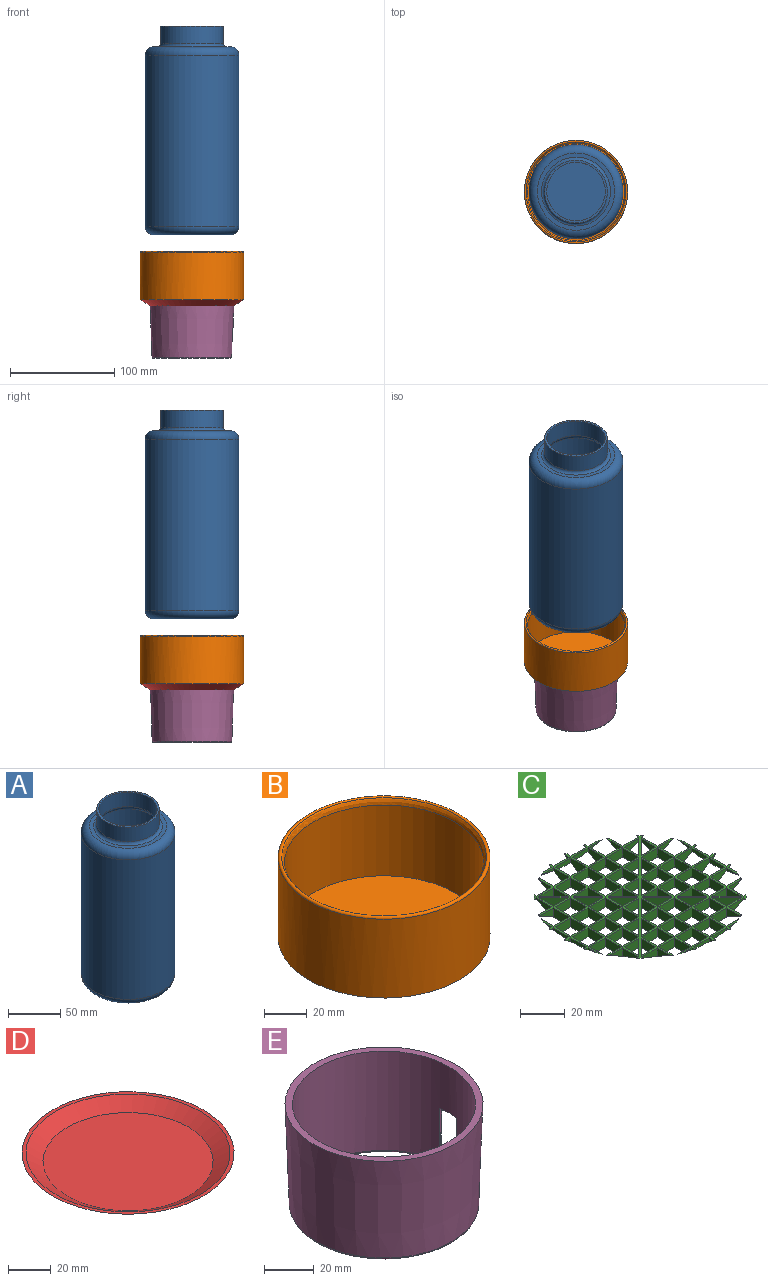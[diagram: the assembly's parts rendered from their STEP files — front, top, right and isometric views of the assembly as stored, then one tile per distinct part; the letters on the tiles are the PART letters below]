
ASSEMBLY  parts=5 mates=4
PART A: 15 faces, bbox 97.4x97.4x200 mm
  f0: plane 74x74mm, normal (0,0,-1), area 879.6mm2, adj f1,f14
  f1: revolved ~86x86mm, area 2359mm2, adj f0,f2
  f2: cylinder r=43mm len=164mm, axis (0,0,1), area 44309mm2, adj f1,f3
  f3: torus R=37mm, axis (0,0,1), area 2417.2mm2, adj f2,f4
  f4: plane 74x74mm, normal (0,0,1), area 4300.8mm2, adj f3
  f5: plane 74x74mm, normal (0,0,-1), area 4300.8mm2, adj f6
  f6: torus R=37mm, axis (0,0,1), area 3323.5mm2, adj f5,f7
  f7: cylinder r=45mm len=164mm, axis (0,0,1), area 46369.9mm2, adj f6,f8
  f8: torus R=37mm, axis (0,0,1), area 3323.5mm2, adj f7,f9
  f9: plane 74x74mm, normal (0,0,1), area 879.6mm2, adj f8,f10
  f10: torus R=33mm, axis (0,0,1), area 920.5mm2, adj f9,f11
  f11: cylinder r=30mm len=60mm, axis (0,0,1), area 3204.4mm2, adj f10,f12
  f12: plane 60x60mm, normal (0,0,1), area 364.4mm2, adj f11,f13
  f13: cylinder r=28mm len=56mm, axis (0,0,1), area 2990.8mm2, adj f12,f14
  f14: torus R=33mm, axis (0,0,1), area 1471.4mm2, adj f0,f13
PART B: 6 faces, bbox 107.2x107.2x46.1 mm
  f0: plane 99x99mm, normal (0,0,-1), area 7697.7mm2, adj f1
  f1: cylinder r=49.5mm len=99mm, axis (0,0,1), area 14015.4mm2, adj f0,f5
  f2: cylinder r=46.5mm len=93mm, axis (0,0,1), area 11808.7mm2, adj f3,f4
  f3: plane 93x93mm, normal (0,0,1), area 6792.9mm2, adj f2
  f4: torus R=51.5mm, axis (0,0,1), area 1065.4mm2, adj f2,f5
  f5: torus R=48.5mm, axis (0,0,-1), area 741.3mm2, adj f1,f4
PART C: 306 faces, bbox 95.5x95.5x5.2 mm
  f0: plane 95.25x95.25mm, normal (0,0,1), area 1422.5mm2, adj f2,f3,f4,f5,f6,f7,f8,f9
  f1: plane 79.42x79.42mm, normal (0,0,-1), area 1003.4mm2, adj f66,f67,f69,f70,f71,f72,f73,f74
  f2: plane 1.96x1.21mm, normal (0,-1,0), area 1.2mm2, adj f0,f297,f298
  f3: plane 1.73x1.06mm, normal (0,1,0), area 0.9mm2, adj f0,f4,f298
  f4: plane 5.68x1.26mm, normal (1,0,0), area 3mm2, adj f0,f3,f298
  f5: plane 8.48x4.6mm, normal (0,1,0), area 19.7mm2, adj f0,f6,f299
  f6: plane 10.01x4.6mm, normal (1,0,0), area 26.7mm2, adj f0,f5,f7,f299
  f7: plane 1.33x0.61mm, normal (0,-1,0), area 0.4mm2, adj f0,f6,f299
  f8: plane 1.33x0.61mm, normal (-1,0,0), area 0.4mm2, adj f0,f9,f299
  f9: plane 10.01x4.6mm, normal (0,1,0), area 26.7mm2, adj f0,f8,f10,f299
  f10: plane 8.48x4.6mm, normal (1,0,0), area 19.7mm2, adj f0,f9,f299
  f11: plane 5.68x1.26mm, normal (0,1,0), area 3mm2, adj f0,f12,f300
  f12: plane 1.73x1.06mm, normal (1,0,0), area 0.9mm2, adj f0,f11,f300
  f13: plane 1.96x1.21mm, normal (-1,0,0), area 1.2mm2, adj f0,f14,f300
  f14: plane 10.01x1.98mm, normal (0,1,0), area 17mm2, adj f0,f13,f15,f300
  f15: plane 3.13x1.97mm, normal (1,0,0), area 3.1mm2, adj f0,f14,f300
  f16: plane 3.13x1.97mm, normal (-1,0,0), area 3.1mm2, adj f0,f17,f300
  f17: plane 10.01x1.98mm, normal (0,1,0), area 17mm2, adj f0,f16,f18,f300
  f18: plane 1.96x1.21mm, normal (1,0,0), area 1.2mm2, adj f0,f17,f300
  f19: plane 1.73x1.06mm, normal (-1,0,0), area 0.9mm2, adj f0,f20,f300
  f20: plane 5.68x1.26mm, normal (0,1,0), area 3mm2, adj f0,f19,f300
  f21: plane 8.48x4.6mm, normal (-1,0,0), area 19.7mm2, adj f0,f22,f301
  f22: plane 10.01x4.6mm, normal (0,1,0), area 26.7mm2, adj f0,f21,f23,f301
  f23: plane 1.33x0.61mm, normal (1,0,0), area 0.4mm2, adj f0,f22,f301
  f24: plane 1.33x0.61mm, normal (0,-1,0), area 0.4mm2, adj f0,f25,f301
  f25: plane 10.01x4.6mm, normal (-1,0,0), area 26.7mm2, adj f0,f24,f26,f301
  f26: plane 8.48x4.6mm, normal (0,1,0), area 19.7mm2, adj f0,f25,f301
  f27: plane 5.68x1.26mm, normal (-1,0,0), area 3mm2, adj f0,f28,f302
  f28: plane 1.73x1.06mm, normal (0,1,0), area 0.9mm2, adj f0,f27,f302
  f29: plane 1.96x1.21mm, normal (0,-1,0), area 1.2mm2, adj f0,f30,f302
  f30: plane 10.01x1.98mm, normal (-1,0,0), area 17mm2, adj f0,f29,f31,f302
  f31: plane 3.13x1.97mm, normal (0,1,0), area 3.1mm2, adj f0,f30,f302
  f32: plane 3.13x1.97mm, normal (0,-1,0), area 3.1mm2, adj f0,f33,f302
  f33: plane 10.01x1.98mm, normal (-1,0,0), area 17mm2, adj f0,f32,f34,f302
  f34: plane 1.96x1.21mm, normal (0,1,0), area 1.2mm2, adj f0,f33,f302
  f35: plane 1.73x1.06mm, normal (0,-1,0), area 0.9mm2, adj f0,f36,f302
  f36: plane 5.68x1.26mm, normal (-1,0,0), area 3mm2, adj f0,f35,f302
  f37: plane 8.48x4.6mm, normal (0,-1,0), area 19.7mm2, adj f0,f38,f303
  f38: plane 10.01x4.6mm, normal (-1,0,0), area 26.7mm2, adj f0,f37,f39,f303
  f39: plane 1.33x0.61mm, normal (0,1,0), area 0.4mm2, adj f0,f38,f303
  f40: plane 1.33x0.61mm, normal (1,0,0), area 0.4mm2, adj f0,f41,f303
  f41: plane 10.01x4.6mm, normal (0,-1,0), area 26.7mm2, adj f0,f40,f42,f303
  f42: plane 8.48x4.6mm, normal (-1,0,0), area 19.7mm2, adj f0,f41,f303
  f43: plane 5.68x1.26mm, normal (0,-1,0), area 3mm2, adj f0,f44,f304
  f44: plane 1.73x1.06mm, normal (-1,0,0), area 0.9mm2, adj f0,f43,f304
  f45: plane 1.96x1.21mm, normal (1,0,0), area 1.2mm2, adj f0,f46,f304
  f46: plane 10.01x1.98mm, normal (0,-1,0), area 17mm2, adj f0,f45,f47,f304
  f47: plane 3.13x1.97mm, normal (-1,0,0), area 3.1mm2, adj f0,f46,f304
  f48: plane 3.13x1.97mm, normal (1,0,0), area 3.1mm2, adj f0,f49,f304
  f49: plane 10.01x1.98mm, normal (0,-1,0), area 17mm2, adj f0,f48,f50,f304
  f50: plane 1.96x1.21mm, normal (-1,0,0), area 1.2mm2, adj f0,f49,f304
  f51: plane 1.73x1.06mm, normal (1,0,0), area 0.9mm2, adj f0,f52,f304
  f52: plane 5.68x1.26mm, normal (0,-1,0), area 3mm2, adj f0,f51,f304
  f53: plane 8.48x4.6mm, normal (1,0,0), area 19.7mm2, adj f0,f54,f305
  f54: plane 10.01x4.6mm, normal (0,-1,0), area 26.7mm2, adj f0,f53,f55,f305
  f55: plane 1.33x0.61mm, normal (-1,0,0), area 0.4mm2, adj f0,f54,f305
  f56: plane 1.33x0.61mm, normal (0,1,0), area 0.4mm2, adj f0,f57,f305
  f57: plane 10.01x4.6mm, normal (1,0,0), area 26.7mm2, adj f0,f56,f58,f305
  f58: plane 8.48x4.6mm, normal (0,-1,0), area 19.7mm2, adj f0,f57,f305
  f59: plane 5.68x1.26mm, normal (1,0,0), area 3mm2, adj f0,f60,f298
  f60: plane 1.73x1.06mm, normal (0,-1,0), area 0.9mm2, adj f0,f59,f298
  f61: plane 1.96x1.21mm, normal (0,1,0), area 1.2mm2, adj f0,f62,f298
  f62: plane 10.01x1.98mm, normal (1,0,0), area 17mm2, adj f0,f61,f63,f298
  f63: plane 3.13x1.97mm, normal (0,-1,0), area 3.1mm2, adj f0,f62,f298
  f64: plane 3.13x1.97mm, normal (0,1,0), area 3.1mm2, adj f0,f297,f298
  f65: plane 7.91x1.68mm, normal (0,1,0), area 7.1mm2, adj f0,f66,f304
  f66: plane 10.1x5.1mm, normal (1,0,0), area 40.9mm2, adj f0,f1,f65,f67,f304
  f67: plane 10x5mm, normal (0,-1,0), area 50mm2, adj f0,f1,f66,f233,f305
  f68: plane 10.01x2.61mm, normal (0,1,0), area 23.3mm2, adj f0,f69,f234,f304
  f69: plane 10.08x5.08mm, normal (1,0,0), area 41.7mm2, adj f0,f1,f68,f70,f304
  f70: plane 10x5mm, normal (0,-1,0), area 50mm2, adj f0,f1,f69,f234
  f71: plane 9.3x9.3mm, normal (-0.71,0.71,0), area 55.3mm2, adj f0,f1,f72,f235,f303
  f72: plane 9.3x5.01mm, normal (1,0,0), area 30.7mm2, adj f0,f1,f71,f235,f303
  f73: plane 9.3x5.01mm, normal (0,1,0), area 30.7mm2, adj f0,f1,f74,f236,f303
  f74: plane 9.3x9.3mm, normal (0.71,-0.71,0), area 55.3mm2, adj f0,f1,f73,f236,f303
  f75: plane 10x5mm, normal (1,0,0), area 50mm2, adj f0,f1,f76,f237
  f76: plane 10x5mm, normal (0,-1,0), area 50mm2, adj f0,f1,f75,f77
  f77: plane 10x5mm, normal (-1,0,0), area 50mm2, adj f0,f1,f76,f237
  f78: plane 10x5mm, normal (-1,0,0), area 50mm2, adj f0,f1,f79,f238
  f79: plane 10x5mm, normal (0,1,0), area 50mm2, adj f0,f1,f78,f80
  f80: plane 10x5mm, normal (1,0,0), area 50mm2, adj f0,f1,f79,f238
  f81: plane 10x5mm, normal (1,0,0), area 50mm2, adj f0,f1,f82,f239
  f82: plane 10x5mm, normal (0,-1,0), area 50mm2, adj f0,f1,f81,f83
  f83: plane 10x5mm, normal (-1,0,0), area 50mm2, adj f0,f1,f82,f239
  f84: plane 9.3x5mm, normal (0,1,0), area 30.7mm2, adj f0,f1,f85,f240,f305
  f85: plane 9.29x5mm, normal (1,0,0), area 46.5mm2, adj f0,f1,f84,f240
  f86: plane 9x4.94mm, normal (0,1,0), area 22.4mm2, adj f0,f87,f305
  f87: plane 10x5mm, normal (1,0,0), area 50mm2, adj f0,f1,f86,f88,f305
  f88: plane 10.1x5.1mm, normal (0,-1,0), area 40.9mm2, adj f0,f1,f87,f241,f298
  f89: plane 10x5mm, normal (0,1,0), area 50mm2, adj f0,f1,f90,f242
  f90: plane 10x5mm, normal (1,0,0), area 50mm2, adj f0,f1,f89,f91
  f91: plane 10x5mm, normal (0,-1,0), area 50mm2, adj f0,f1,f90,f242
  f92: plane 9.29x5mm, normal (0,1,0), area 46.5mm2, adj f0,f1,f93,f243
  f93: plane 9.29x5mm, normal (1,0,0), area 46.5mm2, adj f0,f1,f92,f243
  f94: plane 9.29x5mm, normal (0,1,0), area 46.5mm2, adj f0,f1,f95,f244
  f95: plane 9.29x9.29mm, normal (0.71,-0.71,0), area 65.7mm2, adj f0,f1,f94,f244
  f96: plane 9.29x5mm, normal (-1,0,0), area 46.5mm2, adj f0,f1,f97,f245
  f97: plane 9.29x5mm, normal (0,1,0), area 46.5mm2, adj f0,f1,f96,f245
  f98: plane 10x5mm, normal (0,1,0), area 50mm2, adj f0,f1,f99,f246
  f99: plane 10x5mm, normal (1,0,0), area 50mm2, adj f0,f1,f98,f100
  f100: plane 10x5mm, normal (0,-1,0), area 50mm2, adj f0,f1,f99,f246
  f101: plane 9.29x9.29mm, normal (-0.71,0.71,0), area 65.7mm2, adj f0,f1,f102,f247
  f102: plane 9.29x5mm, normal (1,0,0), area 46.5mm2, adj f0,f1,f101,f247
  f103: plane 10x5mm, normal (0,1,0), area 50mm2, adj f0,f1,f104,f248
  f104: plane 10x5mm, normal (1,0,0), area 50mm2, adj f0,f1,f103,f105
  f105: plane 10x5mm, normal (0,-1,0), area 50mm2, adj f0,f1,f104,f248
  f106: plane 9x4.94mm, normal (0,1,0), area 22.4mm2, adj f0,f249,f303
  f107: plane 7.91x1.68mm, normal (1,0,0), area 7.1mm2, adj f0,f108,f302
  f108: plane 10.1x5.1mm, normal (0,-1,0), area 40.9mm2, adj f0,f1,f107,f249,f302
  f109: plane 10.08x5.08mm, normal (0,1,0), area 41.7mm2, adj f0,f1,f110,f250,f302
  f110: plane 10.01x2.61mm, normal (1,0,0), area 23.3mm2, adj f0,f109,f111,f302
  f111: plane 10x5mm, normal (0,-1,0), area 45.5mm2, adj f0,f1,f110,f250,f302
  f112: plane 10x5mm, normal (0,1,0), area 50mm2, adj f0,f1,f113,f251
  f113: plane 10x5mm, normal (1,0,0), area 50mm2, adj f0,f1,f112,f114
  f114: plane 10x5mm, normal (0,-1,0), area 50mm2, adj f0,f1,f113,f251
  f115: plane 10x5mm, normal (0,1,0), area 50mm2, adj f0,f1,f116,f252
  f116: plane 10x5mm, normal (1,0,0), area 50mm2, adj f0,f1,f115,f117
  f117: plane 10x5mm, normal (0,-1,0), area 50mm2, adj f0,f1,f116,f252
  f118: plane 10x5mm, normal (0,1,0), area 50mm2, adj f0,f1,f119,f253
  f119: plane 10x5mm, normal (1,0,0), area 50mm2, adj f0,f1,f118,f120
  f120: plane 10x5mm, normal (0,-1,0), area 50mm2, adj f0,f1,f119,f253
  f121: plane 10x5mm, normal (0,1,0), area 50mm2, adj f0,f1,f122,f254
  f122: plane 10x5mm, normal (1,0,0), area 50mm2, adj f0,f1,f121,f123
  f123: plane 10x5mm, normal (0,-1,0), area 50mm2, adj f0,f1,f122,f254
  f124: plane 10.08x5.08mm, normal (0,1,0), area 41.7mm2, adj f0,f1,f125,f255,f298
  f125: plane 10x5mm, normal (1,0,0), area 50mm2, adj f0,f1,f124,f126
  f126: plane 10x5mm, normal (0,-1,0), area 45.5mm2, adj f0,f1,f125,f255,f298
  f127: plane 7.91x1.68mm, normal (1,0,0), area 7.1mm2, adj f0,f256,f302
  f128: plane 9x4.94mm, normal (0,-1,0), area 22.4mm2, adj f0,f129,f301
  f129: plane 10x5mm, normal (-1,0,0), area 50mm2, adj f0,f1,f128,f256,f301
  f130: plane 10x5mm, normal (1,0,0), area 50mm2, adj f0,f1,f131,f257
  f131: plane 10x5mm, normal (0,-1,0), area 50mm2, adj f0,f1,f130,f132
  f132: plane 10x5mm, normal (-1,0,0), area 50mm2, adj f0,f1,f131,f257
  f133: plane 9.29x5mm, normal (0,1,0), area 46.5mm2, adj f0,f1,f134,f258
  f134: plane 9.29x5mm, normal (1,0,0), area 46.5mm2, adj f0,f1,f133,f258
  f135: plane 10x5mm, normal (-1,0,0), area 50mm2, adj f0,f1,f136,f259
  f136: plane 10x5mm, normal (0,1,0), area 50mm2, adj f0,f1,f135,f137
  f137: plane 10x5mm, normal (1,0,0), area 50mm2, adj f0,f1,f136,f259
  f138: plane 9.29x9.29mm, normal (-0.71,0.71,0), area 65.7mm2, adj f0,f1,f139,f260
  f139: plane 9.29x5mm, normal (1,0,0), area 46.5mm2, adj f0,f1,f138,f260
  f140: plane 10x5mm, normal (1,0,0), area 50mm2, adj f0,f1,f141,f261
  f141: plane 10x5mm, normal (0,-1,0), area 50mm2, adj f0,f1,f140,f142
  f142: plane 10x5mm, normal (-1,0,0), area 50mm2, adj f0,f1,f141,f261
  f143: plane 10x5mm, normal (1,0,0), area 50mm2, adj f0,f1,f144,f262,f299
  f144: plane 9x4.94mm, normal (0,-1,0), area 22.4mm2, adj f0,f143,f299
  f145: plane 7.91x1.68mm, normal (-1,0,0), area 7.1mm2, adj f0,f262,f298
  f146: plane 9.3x9.3mm, normal (-0.71,0.71,0), area 55.3mm2, adj f0,f1,f147,f263,f299
  f147: plane 9.29x5mm, normal (1,0,0), area 46.5mm2, adj f0,f1,f146,f263
  f148: plane 10x5mm, normal (0,1,0), area 50mm2, adj f0,f1,f149,f264
  f149: plane 10x5mm, normal (1,0,0), area 50mm2, adj f0,f1,f148,f150
  f150: plane 10x5mm, normal (0,-1,0), area 50mm2, adj f0,f1,f149,f264
  f151: plane 10x5mm, normal (0,1,0), area 50mm2, adj f0,f1,f152,f265
  f152: plane 10x5mm, normal (1,0,0), area 50mm2, adj f0,f1,f151,f153
  f153: plane 10x5mm, normal (0,-1,0), area 50mm2, adj f0,f1,f152,f265
  f154: plane 10x5mm, normal (0,1,0), area 50mm2, adj f0,f1,f155,f266
  f155: plane 10x5mm, normal (1,0,0), area 50mm2, adj f0,f1,f154,f156
  f156: plane 10x5mm, normal (0,-1,0), area 50mm2, adj f0,f1,f155,f266
  f157: plane 10x5mm, normal (0,1,0), area 50mm2, adj f0,f1,f158,f267
  f158: plane 10x5mm, normal (1,0,0), area 50mm2, adj f0,f1,f157,f159
  f159: plane 10x5mm, normal (0,-1,0), area 50mm2, adj f0,f1,f158,f267
  f160: plane 9.29x5mm, normal (0,1,0), area 46.5mm2, adj f0,f1,f161,f268
  f161: plane 9.3x5mm, normal (1,0,0), area 30.7mm2, adj f0,f1,f160,f268,f301
  f162: plane 10x5mm, normal (-1,0,0), area 45.5mm2, adj f0,f1,f163,f269,f300
  f163: plane 10x5mm, normal (0,1,0), area 50mm2, adj f0,f1,f162,f164
  f164: plane 10.08x5.08mm, normal (1,0,0), area 41.7mm2, adj f0,f1,f163,f269,f300
  f165: plane 9x4.94mm, normal (1,0,0), area 22.4mm2, adj f0,f270,f301
  f166: plane 7.91x1.68mm, normal (0,-1,0), area 7.1mm2, adj f0,f167,f300
  f167: plane 10.1x5.1mm, normal (-1,0,0), area 40.9mm2, adj f0,f1,f166,f270,f300
  f168: plane 9.29x5mm, normal (0,-1,0), area 46.5mm2, adj f0,f1,f169,f271
  f169: plane 9.29x5mm, normal (-1,0,0), area 46.5mm2, adj f0,f1,f168,f271
  f170: plane 9.29x5mm, normal (1,0,0), area 46.5mm2, adj f0,f1,f171,f272
  f171: plane 9.29x9.29mm, normal (-0.71,-0.71,0), area 65.7mm2, adj f0,f1,f170,f272
  f172: plane 9.29x9.29mm, normal (-0.71,0.71,0), area 65.7mm2, adj f0,f1,f173,f273
  f173: plane 9.29x5mm, normal (1,0,0), area 46.5mm2, adj f0,f1,f172,f273
  f174: plane 9.29x5mm, normal (-1,0,0), area 46.5mm2, adj f0,f1,f175,f274
  f175: plane 9.29x5mm, normal (0,1,0), area 46.5mm2, adj f0,f1,f174,f274
  f176: plane 9.29x5mm, normal (0,1,0), area 46.5mm2, adj f0,f1,f177,f275
  f177: plane 9.29x5mm, normal (1,0,0), area 46.5mm2, adj f0,f1,f176,f275
  f178: plane 9.29x5mm, normal (1,0,0), area 46.5mm2, adj f0,f1,f179,f276
  f179: plane 9.29x5mm, normal (0,-1,0), area 46.5mm2, adj f0,f1,f178,f276
  f180: plane 9.29x9.29mm, normal (0.71,0.71,0), area 65.7mm2, adj f0,f1,f181,f277
  f181: plane 9.29x5mm, normal (0,-1,0), area 46.5mm2, adj f0,f1,f180,f277
  f182: plane 10x5mm, normal (0,1,0), area 50mm2, adj f0,f1,f183,f278
  f183: plane 10x5mm, normal (1,0,0), area 45.5mm2, adj f0,f1,f182,f184,f300
  f184: plane 10.01x2.61mm, normal (0,-1,0), area 23.3mm2, adj f0,f183,f278,f300
  f185: plane 7.91x1.68mm, normal (0,-1,0), area 7.1mm2, adj f0,f279,f300
  f186: plane 9x4.94mm, normal (-1,0,0), area 22.4mm2, adj f0,f187,f299
  f187: plane 10x5mm, normal (0,1,0), area 50mm2, adj f0,f1,f186,f279,f299
  f188: plane 9.3x5.01mm, normal (0,-1,0), area 30.7mm2, adj f0,f1,f189,f280,f301
  f189: plane 9.29x5mm, normal (-1,0,0), area 46.5mm2, adj f0,f1,f188,f280
  f190: plane 9.29x5mm, normal (0,1,0), area 46.5mm2, adj f0,f1,f191,f281
  f191: plane 9.3x9.3mm, normal (0.71,-0.71,0), area 55.3mm2, adj f0,f1,f190,f281,f299
  f192: plane 9.29x5mm, normal (0,1,0), area 46.5mm2, adj f0,f1,f193,f282
  f193: plane 9.29x9.29mm, normal (0.71,-0.71,0), area 65.7mm2, adj f0,f1,f192,f282
  f194: plane 10x5mm, normal (0,1,0), area 50mm2, adj f0,f1,f195,f283
  f195: plane 10x5mm, normal (1,0,0), area 50mm2, adj f0,f1,f194,f196
  f196: plane 10x5mm, normal (0,-1,0), area 50mm2, adj f0,f1,f195,f283
  f197: plane 9.29x9.29mm, normal (0.71,0.71,0), area 65.7mm2, adj f0,f1,f198,f284
  f198: plane 9.29x5mm, normal (0,-1,0), area 46.5mm2, adj f0,f1,f197,f284
  f199: plane 10x5mm, normal (-1,0,0), area 50mm2, adj f0,f1,f200,f285
  f200: plane 10x5mm, normal (0,1,0), area 45.5mm2, adj f0,f1,f199,f201,f302
  f201: plane 10.01x2.61mm, normal (1,0,0), area 23.3mm2, adj f0,f200,f285,f302
  f202: plane 10x5mm, normal (-1,0,0), area 50mm2, adj f0,f1,f203,f286
  f203: plane 10x5mm, normal (0,1,0), area 50mm2, adj f0,f1,f202,f204
  f204: plane 10x5mm, normal (1,0,0), area 50mm2, adj f0,f1,f203,f286
  f205: plane 10x5mm, normal (-1,0,0), area 50mm2, adj f0,f1,f206,f287
  f206: plane 10x5mm, normal (0,1,0), area 50mm2, adj f0,f1,f205,f207
  f207: plane 10x5mm, normal (1,0,0), area 50mm2, adj f0,f1,f206,f287
  f208: plane 10x5mm, normal (-1,0,0), area 50mm2, adj f0,f1,f209,f288
  f209: plane 10x5mm, normal (0,1,0), area 50mm2, adj f0,f1,f208,f210
  f210: plane 10x5mm, normal (1,0,0), area 50mm2, adj f0,f1,f209,f288
  f211: plane 10x5mm, normal (-1,0,0), area 50mm2, adj f0,f1,f212,f289
  f212: plane 10x5mm, normal (0,1,0), area 50mm2, adj f0,f1,f211,f213
  f213: plane 10x5mm, normal (1,0,0), area 50mm2, adj f0,f1,f212,f289
  f214: plane 10.01x2.61mm, normal (-1,0,0), area 23.3mm2, adj f0,f215,f290,f298
  f215: plane 10x5mm, normal (0,1,0), area 45.5mm2, adj f0,f1,f214,f216,f298
  f216: plane 10x5mm, normal (1,0,0), area 50mm2, adj f0,f1,f215,f290
  f217: plane 10x5mm, normal (0,1,0), area 50mm2, adj f0,f1,f218,f291
  f218: plane 10x5mm, normal (1,0,0), area 50mm2, adj f0,f1,f217,f219
  f219: plane 10x5mm, normal (0,-1,0), area 50mm2, adj f0,f1,f218,f291
  f220: plane 9.29x5mm, normal (0,-1,0), area 46.5mm2, adj f0,f1,f221,f292
  f221: plane 9.29x5mm, normal (-1,0,0), area 46.5mm2, adj f0,f1,f220,f292
  f222: plane 9.3x9.3mm, normal (0.71,0.71,0), area 55.3mm2, adj f0,f1,f223,f293,f305
  f223: plane 9.29x5mm, normal (0,-1,0), area 46.5mm2, adj f0,f1,f222,f293
  f224: plane 10x5mm, normal (0,1,0), area 50mm2, adj f0,f1,f225,f294
  f225: plane 10x5mm, normal (1,0,0), area 50mm2, adj f0,f1,f224,f226
  f226: plane 10x5mm, normal (0,-1,0), area 50mm2, adj f0,f1,f225,f294
  f227: plane 10x5mm, normal (0,-1,0), area 50mm2, adj f0,f1,f228,f295,f303
  f228: plane 10.1x5.1mm, normal (-1,0,0), area 40.9mm2, adj f0,f1,f227,f229,f304
  f229: plane 7.91x1.68mm, normal (0,1,0), area 7.1mm2, adj f0,f228,f304
  f230: plane 10.01x2.61mm, normal (0,1,0), area 23.3mm2, adj f0,f231,f296,f304
  f231: plane 10x5mm, normal (1,0,0), area 45.5mm2, adj f0,f1,f230,f232,f304
  f232: plane 10x5mm, normal (0,-1,0), area 50mm2, adj f0,f1,f231,f296
  f233: plane 9x4.94mm, normal (-1,0,0), area 22.4mm2, adj f0,f67,f305
  f234: plane 10x5mm, normal (-1,0,0), area 45.5mm2, adj f0,f1,f68,f70,f304
  f235: plane 9.29x5mm, normal (0,-1,0), area 46.5mm2, adj f0,f1,f71,f72
  f236: plane 9.29x5mm, normal (-1,0,0), area 46.5mm2, adj f0,f1,f73,f74
  f237: plane 10x5mm, normal (0,1,0), area 50mm2, adj f0,f1,f75,f77
  f238: plane 10x5mm, normal (0,-1,0), area 50mm2, adj f0,f1,f78,f80
  f239: plane 10x5mm, normal (0,1,0), area 50mm2, adj f0,f1,f81,f83
  f240: plane 9.3x9.3mm, normal (-0.71,-0.71,0), area 55.3mm2, adj f0,f1,f84,f85,f305
  f241: plane 7.91x1.68mm, normal (-1,0,0), area 7.1mm2, adj f0,f88,f298
  f242: plane 10x5mm, normal (-1,0,0), area 50mm2, adj f0,f1,f89,f91
  f243: plane 9.29x9.29mm, normal (-0.71,-0.71,0), area 65.7mm2, adj f0,f1,f92,f93
  f244: plane 9.29x5mm, normal (-1,0,0), area 46.5mm2, adj f0,f1,f94,f95
  f245: plane 9.29x9.29mm, normal (0.71,-0.71,0), area 65.7mm2, adj f0,f1,f96,f97
  f246: plane 10x5mm, normal (-1,0,0), area 50mm2, adj f0,f1,f98,f100
  f247: plane 9.29x5mm, normal (0,-1,0), area 46.5mm2, adj f0,f1,f101,f102
  f248: plane 10x5mm, normal (-1,0,0), area 50mm2, adj f0,f1,f103,f105
  f249: plane 10x5mm, normal (-1,0,0), area 50mm2, adj f0,f1,f106,f108,f303
  f250: plane 10x5mm, normal (-1,0,0), area 50mm2, adj f0,f1,f109,f111
  f251: plane 10x5mm, normal (-1,0,0), area 50mm2, adj f0,f1,f112,f114
  f252: plane 10x5mm, normal (-1,0,0), area 50mm2, adj f0,f1,f115,f117
  f253: plane 10x5mm, normal (-1,0,0), area 50mm2, adj f0,f1,f118,f120
  f254: plane 10x5mm, normal (-1,0,0), area 50mm2, adj f0,f1,f121,f123
  f255: plane 10.01x2.61mm, normal (-1,0,0), area 23.3mm2, adj f0,f124,f126,f298
  f256: plane 10.1x5.1mm, normal (0,1,0), area 40.9mm2, adj f0,f1,f127,f129,f302
  f257: plane 10x5mm, normal (0,1,0), area 50mm2, adj f0,f1,f130,f132
  f258: plane 9.29x9.29mm, normal (-0.71,-0.71,0), area 65.7mm2, adj f0,f1,f133,f134
  f259: plane 10x5mm, normal (0,-1,0), area 50mm2, adj f0,f1,f135,f137
  f260: plane 9.29x5mm, normal (0,-1,0), area 46.5mm2, adj f0,f1,f138,f139
  f261: plane 10x5mm, normal (0,1,0), area 50mm2, adj f0,f1,f140,f142
  f262: plane 10.1x5.1mm, normal (0,1,0), area 40.9mm2, adj f0,f1,f143,f145,f298
  f263: plane 9.3x5mm, normal (0,-1,0), area 30.7mm2, adj f0,f1,f146,f147,f299
  f264: plane 10x5mm, normal (-1,0,0), area 50mm2, adj f0,f1,f148,f150
  f265: plane 10x5mm, normal (-1,0,0), area 50mm2, adj f0,f1,f151,f153
  f266: plane 10x5mm, normal (-1,0,0), area 50mm2, adj f0,f1,f154,f156
  f267: plane 10x5mm, normal (-1,0,0), area 50mm2, adj f0,f1,f157,f159
  f268: plane 9.3x9.3mm, normal (-0.71,-0.71,0), area 55.3mm2, adj f0,f1,f160,f161,f301
  f269: plane 10.01x2.61mm, normal (0,-1,0), area 23.3mm2, adj f0,f162,f164,f300
  f270: plane 10x5mm, normal (0,1,0), area 50mm2, adj f0,f1,f165,f167,f301
  f271: plane 9.29x9.29mm, normal (0.71,0.71,0), area 65.7mm2, adj f0,f1,f168,f169
  f272: plane 9.29x5mm, normal (0,1,0), area 46.5mm2, adj f0,f1,f170,f171
  f273: plane 9.29x5mm, normal (0,-1,0), area 46.5mm2, adj f0,f1,f172,f173
  f274: plane 9.29x9.29mm, normal (0.71,-0.71,0), area 65.7mm2, adj f0,f1,f174,f175
  f275: plane 9.29x9.29mm, normal (-0.71,-0.71,0), area 65.7mm2, adj f0,f1,f176,f177
  f276: plane 9.29x9.29mm, normal (-0.71,0.71,0), area 65.7mm2, adj f0,f1,f178,f179
  f277: plane 9.29x5mm, normal (-1,0,0), area 46.5mm2, adj f0,f1,f180,f181
  f278: plane 10.08x5.08mm, normal (-1,0,0), area 41.7mm2, adj f0,f1,f182,f184,f300
  f279: plane 10.1x5.1mm, normal (1,0,0), area 40.9mm2, adj f0,f1,f185,f187,f300
  f280: plane 9.3x9.3mm, normal (0.71,0.71,0), area 55.3mm2, adj f0,f1,f188,f189,f301
  f281: plane 9.3x5mm, normal (-1,0,0), area 30.7mm2, adj f0,f1,f190,f191,f299
  f282: plane 9.29x5mm, normal (-1,0,0), area 46.5mm2, adj f0,f1,f192,f193
  f283: plane 10x5mm, normal (-1,0,0), area 50mm2, adj f0,f1,f194,f196
  f284: plane 9.29x5mm, normal (-1,0,0), area 46.5mm2, adj f0,f1,f197,f198
  f285: plane 10.08x5.08mm, normal (0,-1,0), area 41.7mm2, adj f0,f1,f199,f201,f302
  f286: plane 10x5mm, normal (0,-1,0), area 50mm2, adj f0,f1,f202,f204
  f287: plane 10x5mm, normal (0,-1,0), area 50mm2, adj f0,f1,f205,f207
  f288: plane 10x5mm, normal (0,-1,0), area 50mm2, adj f0,f1,f208,f210
  f289: plane 10x5mm, normal (0,-1,0), area 50mm2, adj f0,f1,f211,f213
  f290: plane 10.08x5.08mm, normal (0,-1,0), area 41.7mm2, adj f0,f1,f214,f216,f298
  f291: plane 10x5mm, normal (-1,0,0), area 50mm2, adj f0,f1,f217,f219
  f292: plane 9.29x9.29mm, normal (0.71,0.71,0), area 65.7mm2, adj f0,f1,f220,f221
  f293: plane 9.3x5.01mm, normal (-1,0,0), area 30.7mm2, adj f0,f1,f222,f223,f305
  f294: plane 10x5mm, normal (-1,0,0), area 50mm2, adj f0,f1,f224,f226
  f295: plane 9x4.94mm, normal (1,0,0), area 22.4mm2, adj f0,f227,f303
  f296: plane 10.08x5.08mm, normal (-1,0,0), area 41.7mm2, adj f0,f1,f230,f232,f304
  f297: plane 10.01x1.98mm, normal (1,0,0), area 17mm2, adj f0,f2,f64,f298
  f298: cone r=39.71mm half-angle=57.7deg, axis (0,0,1), area 69.1mm2, adj f0,f1,f2,f3,f4,f59,f60,f61
  f299: cone r=39.71mm half-angle=57.7deg, axis (0,0,1), area 55.7mm2, adj f0,f1,f5,f6,f7,f8,f9,f10
  f300: cone r=39.71mm half-angle=57.7deg, axis (0,0,1), area 69.1mm2, adj f0,f1,f11,f12,f13,f14,f15,f16
  f301: cone r=39.71mm half-angle=57.7deg, axis (0,0,1), area 55.7mm2, adj f0,f1,f21,f22,f23,f24,f25,f26
  f302: cone r=39.71mm half-angle=57.7deg, axis (0,0,1), area 69.1mm2, adj f0,f1,f27,f28,f29,f30,f31,f32
  f303: cone r=39.71mm half-angle=57.7deg, axis (0,0,1), area 55.7mm2, adj f0,f1,f37,f38,f39,f40,f41,f42
  f304: cone r=39.71mm half-angle=57.7deg, axis (0,0,1), area 69.1mm2, adj f0,f1,f43,f44,f45,f46,f47,f48
  f305: cone r=39.71mm half-angle=57.7deg, axis (0,0,1), area 55.7mm2, adj f0,f1,f53,f54,f55,f56,f57,f58
PART D: 5 faces, bbox 99x99x6 mm
  f0: plane 79.42x79.42mm, normal (0,0,1), area 4954.1mm2, adj f4
  f1: plane 80x80mm, normal (0,0,-1), area 5026.5mm2, adj f2
  f2: cone r=40mm half-angle=57.7deg, axis (0,0,1), area 3159.3mm2, adj f1,f3
  f3: plane 99x99mm, normal (0,0,1), area 571.4mm2, adj f2,f4
  f4: cone r=39.71mm half-angle=57.7deg, axis (0,0,1), area 2569.1mm2, adj f0,f3
PART E: 11 faces, bbox 82.5x82.9x97.2 mm
  f0: plane 80x80mm, normal (0,0,1), area 725.7mm2, adj f1,f2
  f1: cylinder r=37mm len=74mm, axis (0,0,1), area 11137.8mm2, adj f0,f3,f4,f5,f6
  f2: cone r=40mm half-angle=2deg, axis (0,0,1), area 11735.6mm2, adj f0,f7,f8,f9,f10
  f3: plane 9.98x1.55mm, normal (0,0,-1), area 12.2mm2, adj f1,f4,f5,f8,f9,f10
  f4: plane 26.84x1.18mm, normal (0.13,0.99,0), area 19.3mm2, adj f1,f3,f6,f10
  f5: plane 26.84x1.18mm, normal (0.13,-0.99,0), area 19.3mm2, adj f1,f3,f6,f8
  f6: torus R=38mm, axis (0,0,1), area 270.5mm2, adj f1,f4,f5,f7,f8,f10
  f7: torus R=37.29mm, axis (0,0,1), area 267.3mm2, adj f2,f6,f8,f10
  f8: bspline ~97.24x4.38mm, area 43.4mm2, adj f2,f3,f5,f6,f7,f9
  f9: torus R=38.24mm, axis (0,0,-1), area 17.2mm2, adj f2,f3,f8,f10
  f10: bspline ~97.24x4.38mm, area 43.4mm2, adj f2,f3,f4,f6,f7,f9
PLACE A t=(-68.25,-20.98,58.16)mm
PLACE B t=(-68.25,-20.98,-1.84)mm
PLACE C t=(-68.25,-20.98,-1.84)mm
PLACE D t=(-68.25,-20.98,-1.84)mm
PLACE E t=(-68.25,-20.98,-1.84)mm
MATE slider A.f2 <-> B.f1  axis (0,0,-1) through (-68.25,-20.98,58.16)mm
MATE fastened E.f1 <-> D.f2  axis (0,0,1) through (-68.25,-20.98,-9.84)mm
MATE fastened B.f1 <-> C.f298  axis (0,0,-1) through (-68.25,-20.98,-3.84)mm
MATE fastened C.f298 <-> D.f2  axis (0,0,-1) through (-68.25,-20.98,-8.84)mm
